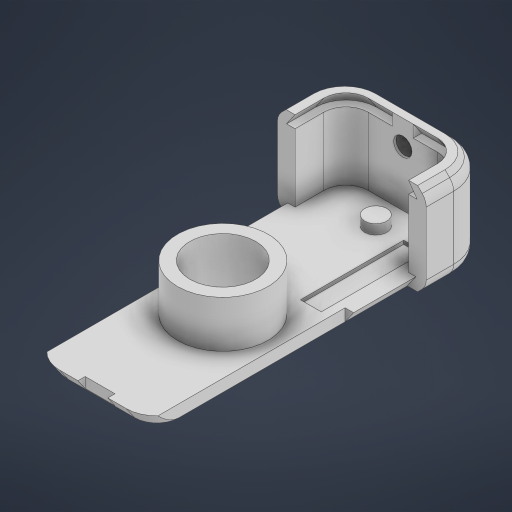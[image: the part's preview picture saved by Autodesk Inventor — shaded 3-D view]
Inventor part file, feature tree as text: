
AUTODESK INVENTOR PART (.ipt)
format: ipt  version: 2023 (Build 270158000, 158)  size: 483,328 bytes
history: native  units: in
note: dims shown in document units (in); Inventor stores cm internally (conversion verified against a paired STEP export)
features: extrude x10, sketch x9, move_body x5, direct_edit x3, sweep x2, chamfer x2, fillet x1
ambient origin geometry x8: Origin, YZ Plane, XZ Plane, XY Plane, X Axis, Y Axis, Z Axis, Center Point
bodies: Solid1 (feature_tree)
feature tree (32):
  extrude  "Extrusion1"  Depth=0.0079in
  extrude  "Extrusion2"  Depth=0.2657in TaperAngle=0.0deg
  direct_edit  "Direct Edit1"
  sketch  "Sketch5"  dims[d1=0.6299in d2=0.0079in]
  sweep  "Sweep1"
  sweep  "Sweep2"
  extrude  "Extrusion13"  Depth=0.0689in
  chamfer  "Chamfer2"  [1 undecoded]
  fillet  "Fillet1"  [1 undecoded]
  direct_edit  "Direct Edit3"
  sketch  "Sketch7"  dims[d13=0.1181in d27=0.5157in]
  extrude  "Extrusion14"  TaperAngle=0.0deg  [1 undecoded]
  direct_edit  "Direct Edit4"
  extrude  "Extrusion18"  Depth=0.0787in
  extrude  "Extrusion15"  TaperAngle=0.0deg  [1 undecoded]
  extrude  "Extrusion16"  TaperAngle=0.0deg  [1 undecoded]
  extrude  "Extrusion17"  TaperAngle=0.0deg  [1 undecoded]
  extrude  "Extrusion19"  Depth=0.0551in
  chamfer  "Chamfer3"  Distance=0.1693in
  extrude  "Extrusion20"  Depth=0.0551in
  sketch  "3D Sketch1"
  sketch  "3D Sketch4"
  sketch  "Sketch6"  dims[d7=0.0689in d8=0.0in d9=0.2657in d10=0.0in]
  sketch  "Sketch8"  dims[d28=0.374in d47=0.0in d48=0.0in d49=0.189in]
  sketch  "Sketch9"  dims[d50=0.3779in d51=0.0689in d52=0.0in d53=0.0in d54=0.0in d55=0.0in]
  sketch  "Sketch10"  dims[d58=0.1693in d59=0.0in d60=0.0in]
  sketch  "Sketch11"  dims[d61=0.0492in d62=0.0787in d63=45.0deg d64=0.0787in d70=0.0in d71=0.0in d72=-0.0059in d73=0.0in d74=0.0in d75=-0.0059in d76=0.0in d77=0.0in d78=-0.0059in d80=0.1398in d81=0.1693in d82=0.1043in d83=0.3937in d84=0.0in d85=0.0787in d86=0.0in d87=0.0in d88=0.0in d89=-0.5709in d90=0.3543in d91=0.0in d92=0.0in d93=0.2087in d94=0.2165in d96=0.8031in d97=0.1181in d98=0.0197in d99=0.0in d100=0.1181in d101=0.0197in d102=0.0in d104=0.5217in d105=0.4291in d107=1.0157in d109=0.1004in d110=0.0925in d111=0.1181in d112=0.2165in d113=0.1181in d114=0.0591in d115=0.0in d116=0.0591in d117=0.0787in d118=45.0deg d119=0.126in d120=0.0906in d121=0.0551in d122=0.0in d11=0.0197in d12=0.0344in d33=0.0197in d34=0.0344in d35=0.0197in d36=0.0344in d65=0.0197in d66=0.0344in d67=0.0197in d68=0.0344in d103=0.0197in d106=0.0344in]
  move_body  "Move1"
  move_body  "Move3"
  move_body  "Move4"
  move_body  "Move5"
  move_body  "Move6"
note: 6 required parameter values undecoded (feature->parameter linkage not recoverable at this tier; creation-order binding heuristic only, values carry confidence <= 0.55)
